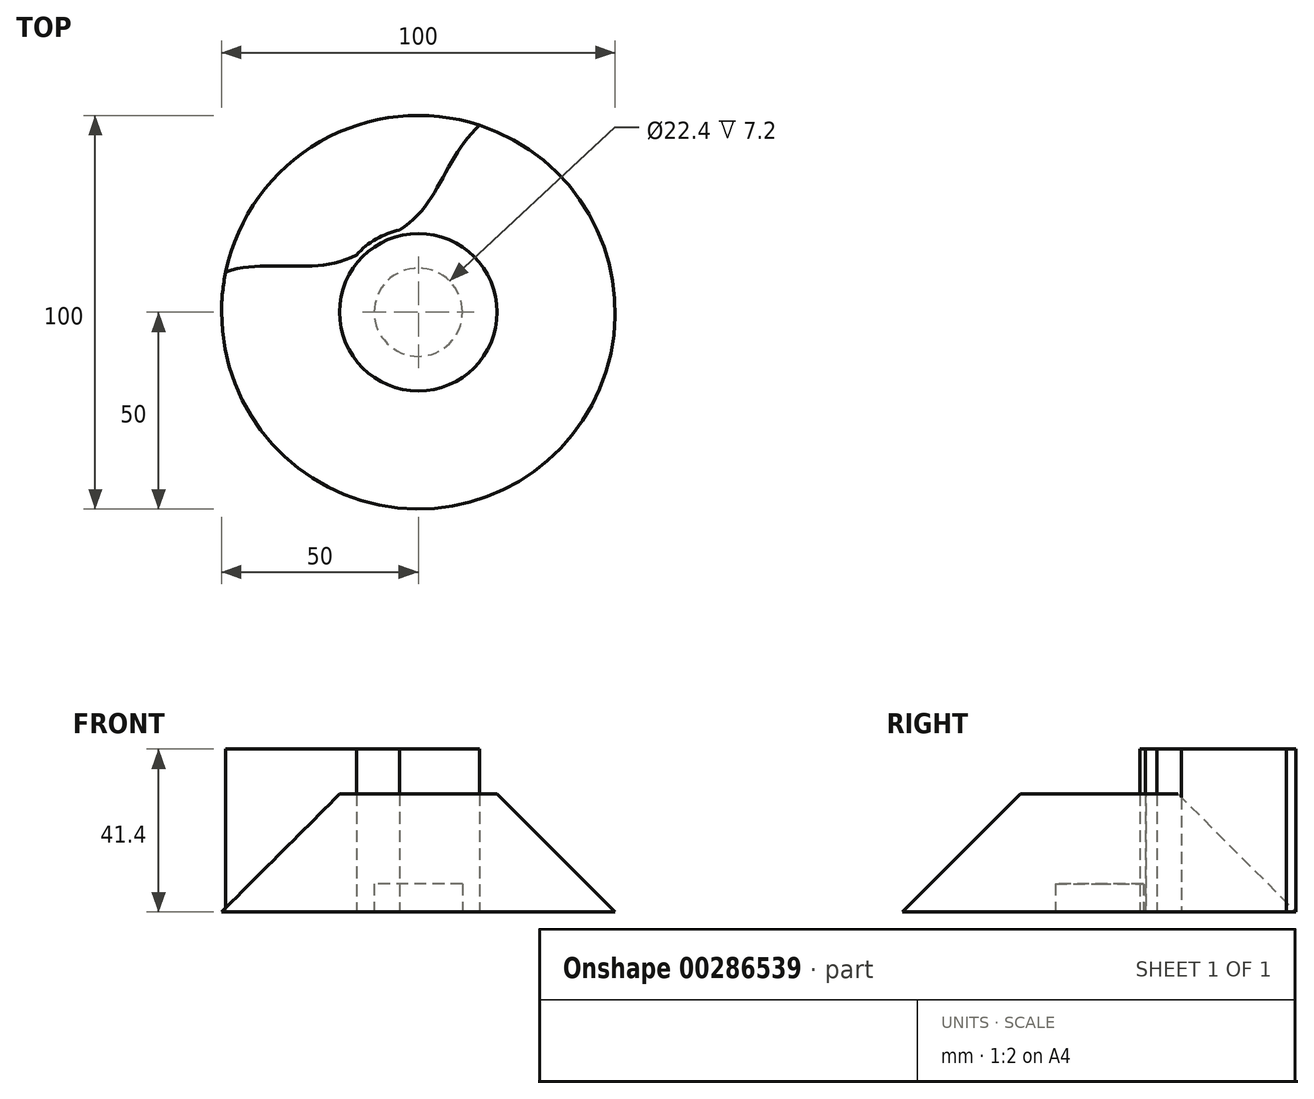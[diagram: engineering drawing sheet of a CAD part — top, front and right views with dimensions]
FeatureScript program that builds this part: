
annotation { "Feature Type Name" : "Feature", "Feature Type Description" : "" }
export const myFeature = defineFeature(function(context is Context, id is Id, definition is map)
    precondition{}
    {
        {
            var Q0;
            Q0=qCreatedBy(makeId("Front.planeOp"),FACE);
            var sketch = newSketch(context, id + "F0", { "sketchPlane" : qUnion([Q0])});
            skLineSegment(sketch, "E0", {"start": v(0, 30) * mm, "end": v(20, 30) * mm});
            skLineSegment(sketch, "E1", {"start": v(20, 30) * mm, "end": v(50, 0) * mm});
            skLineSegment(sketch, "E2", {"start": v(50, 0) * mm, "end": v(0, 0) * mm});
            skLineSegment(sketch, "E3", {"start": v(0, 0) * mm, "end": v(0, 30) * mm});
            skSolve(sketch);
        }
        {
            var Q0;
            Q0=makeQuery(id+"F0.imprint","IMPRINT",FACE,{"disambiguationData":[TD([[makeQuery(id+"F0.imprint","IMPRINT",EDGE,{"derivedFrom":sQuery(id+"F0.wireOp",EDGE,"E0")}),-1.0]])]});
            var Q1;
            Q1=sQuery(id+"F0.wireOp",EDGE,"E3");
            revolve(context, id + "F1", {"entities" : qUnion([Q0]), "axis" : qUnion([Q1]), "revolveType" : RevolveType.FULL});
        }
        {
            var Q0;
            Q0=qCreatedBy(makeId("Top.planeOp"),FACE);
            var sketch = newSketch(context, id + "F2", { "sketchPlane" : qUnion([Q0])});
            skCircle(sketch, "E4", {"center": v(0, 0) * mm, "radius": 11 * mm});
            skSolve(sketch);
        }
        {
            var Q0;
            Q0 = qSketchRegion(id + "F2", true);
            extrude(context, id + "F3", {"entities" : qUnion([Q0]), "depth" : 7 * mm});
        }
        {
            var Q0;
            Q0=makeQuery(id+"F3.opExtrude","SWEPT_BODY",BODY,{"disambiguationData":[OSD([sQuery(id+"F2.wireOp",EDGE,"E4")])]});
            var Q1;
            Q1=makeQuery(id+"F1.opRevolve","SWEPT_BODY",BODY,{"disambiguationData":[OSD([sQuery(id+"F0.wireOp",EDGE,"E0"),sQuery(id+"F0.wireOp",EDGE,"E1"),sQuery(id+"F0.wireOp",EDGE,"E2"),sQuery(id+"F0.wireOp",EDGE,"E3")])]});
            booleanBodies(context, id + "F4", {"operationType" : BooleanOperationType.SUBTRACTION, "tools" : qUnion([Q0]), "targets" : qUnion([Q1]), "offset" : true, "offsetAll" : true, "offsetDistance" : .2 * mm});
        }
        {
            var Q0;
            Q0=makeQuery(id+"F1.opRevolve","SWEPT_FACE",FACE,{"disambiguationData":[OSD([sQuery(id+"F0.wireOp",EDGE,"E2")])]});
            var sketch = newSketch(context, id + "F5", { "sketchPlane" : qUnion([Q0])});
            skLineSegment(sketch, "E5", {"start": v(0, 0) * mm, "end": v(-25, -43.3) * mm, "construction": true});
            skCircle(sketch, "E6", {"center": v(0, 0) * mm, "radius": 21.45 * mm});
            skFitSpline(sketch, "E7", {"points": [v(-48.94, -10.25) * mm, v(-15.72, -14.59) * mm], "startDerivative": vector(33.28, -11.26) * mm, "endDerivative": vector(30.99, -17.04) * mm});
            skFitSpline(sketch, "E8.MirrorCS", {"points": [v(15.59, -47.5) * mm, v(-4.77, -20.91) * mm], "startDerivative": vector(-26.39, 23.2) * mm, "endDerivative": vector(-30.25, 18.32) * mm});
            skArc(sketch, "E9", {"start": v(15.59, -47.5) * mm, "mid": v(-25, -43.3) * mm, "end": v(-48.94, -10.25) * mm});
            skSolve(sketch);
        }
        {
            var Q0;
            {var subQ0=sQuery(id+"F5.wireOp",EDGE,"E7");Q0=makeQuery(id+"F5.imprint","IMPRINT",FACE,{"disambiguationData":[TD([[makeQuery(id+"F5.imprint","IMPRINT",EDGE,{"derivedFrom":subQ0}),-1.0]])]});}
            extrude(context, id + "F6", {"entities" : qUnion([Q0]), "oppositeDirection" : true, "depth" : 41.4 * mm});
        }
    });
